# Revit family: ID310
name_source: partatom
category: Apparecchi idraulici
units: mm (PartAtom-declared; Revit-internal decimal feet)

## family parameters
Basato su piano di lavoro = No
Condiviso = No
Mantieni orientamento annotazione = No
Numero OmniClass = 23.45.55.17
Punto di calcolo locali = No
Quota connettore circolare = Usa diametro
Sempre verticale = Sì
Taglio con vuoti quando caricato = No
Tipo di parte = Normale
Titolo OmniClass = Mixing Faucets

## types (12) — shared parameters
Cold water inlet = 10 mm  [stored 0.0328084 ft]
Commenti sul tipo = Wall mixer
Connessione CW = No
Connessione HW = No
Connessione di scarico = No
Connessione di ventilazione = No
Descrizione = Exposed parts for manual wall mixer with two ways diverter
Hot water inlet = 10 mm  [stored 0.0328084 ft]
Produttore = IB Rubinetterie S.p.A.
URL = https://www.weareib.it
zero-valued in all types: Prospetto di default

## per-type parameters (varying)
| type | Finishes surface | Immagine tipo | Modello |
| Chrome | IB_Chrome | ID310CC.jpg | ID310CC |
| Brushed nickel | IB_Brushed nickel | ID310SS.jpg | ID310SS |
| Natural brass | IB_Brass | ID310ON.jpg | ID310ON |
| Matt black | IB_matt black | ID310NP.jpg | ID310NP |
| Black chrome | IB_Black chrome | ID310CF.jpg | ID310CF |
| Brushed black chrome | IB_Brushed black chrome | ID310CS.jpg | ID310CS |
| Pale gold | IB_Pale gold | ID310II.jpg | ID310II |
| Brushed pale gold | IB_brushed pale gold | ID310IS.jpg | ID310IS |
| Rose gold | IB_Rose gold | ID310RS.jpg | ID310RS |
| Brushed rose gold | IB_Brushed rose gold | ID310SR.jpg | ID310SR |
| Gold | IB_gold | ID310OO.jpg | ID310OO |
| Brushed gold | IB_brushed gold | ID310OS.jpg | ID310OS |

note: [stored X ft] marks values corroborated as IEEE doubles in the binary element streams (Revit-internal decimal feet)
